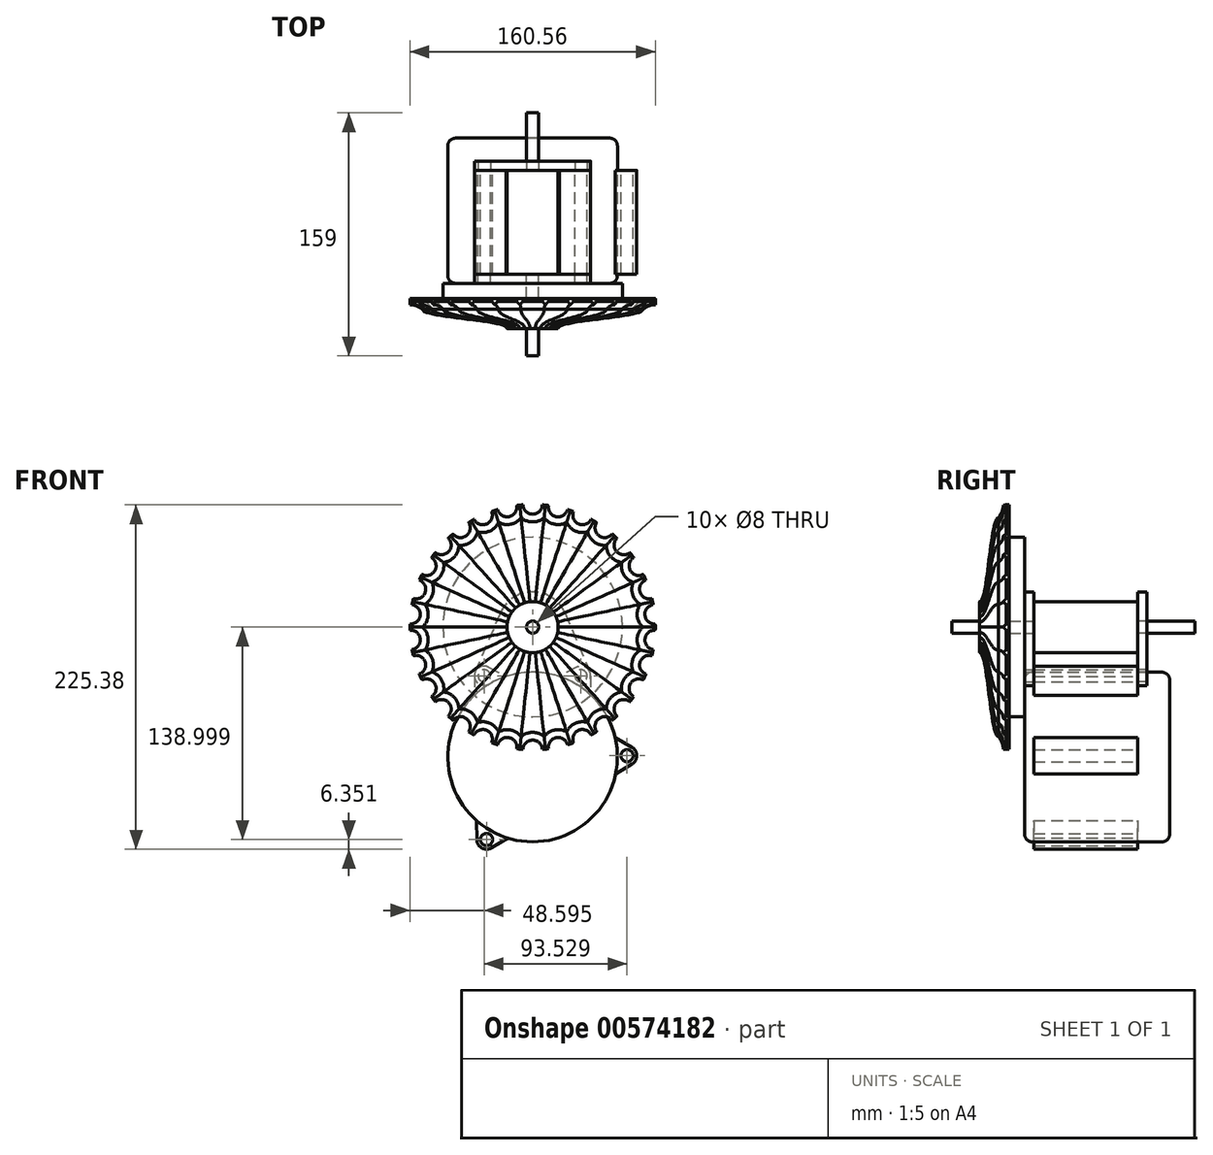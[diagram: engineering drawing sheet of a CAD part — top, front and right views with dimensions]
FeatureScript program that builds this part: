
annotation { "Feature Type Name" : "Feature", "Feature Type Description" : "" }
export const myFeature = defineFeature(function(context is Context, id is Id, definition is map)
    precondition{}
    {
        {
            var Q0;
            Q0=qCreatedBy(makeId("Front.planeOp"),FACE);
            var sketch = newSketch(context, id + "F0", { "sketchPlane" : qUnion([Q0])});
            skCircle(sketch, "E0", {"center": v(0, 0) * mm, "radius": 4 * mm});
            skCircle(sketch, "E1", {"center": v(0, 0) * mm, "radius": 16.75 * mm});
            skCircle(sketch, "E2", {"center": v(0, 0) * mm, "radius": 58.75 * mm, "construction": true});
            skLineSegment(sketch, "E3", {"start": v(0, 58.75) * mm, "end": v(0, -140.5) * mm, "construction": true});
            skCircle(sketch, "E4", {"center": v(0, -85) * mm, "radius": 55.5 * mm});
            skArc(sketch, "E5", {"start": v(28.43, -37.34) * mm, "mid": v(38.03, -32.02) * mm, "end": v(28.67, -26.3) * mm});
            skArc(sketch, "E6", {"start": v(-28.67, -26.3) * mm, "mid": v(-38.03, -32.02) * mm, "end": v(-28.43, -37.34) * mm});
            skArc(sketch, "E7.1.0", {"start": v(-36.5, -139.18) * mm, "mid": v(-33.25, -144.54) * mm, "end": v(-26.98, -144.5) * mm});
            skArc(sketch, "E7.2.0", {"start": v(65.17, -89.53) * mm, "mid": v(68.2, -84.03) * mm, "end": v(65.02, -78.62) * mm});
            skCircle(sketch, "E8", {"center": v(31.69, -31.88) * mm, "radius": 4 * mm});
            skCircle(sketch, "E9", {"center": v(-31.69, -31.88) * mm, "radius": 4 * mm});
            skCircle(sketch, "E10.1.0", {"center": v(-30.16, -139) * mm, "radius": 4 * mm});
            skCircle(sketch, "E10.2.0", {"center": v(61.84, -84.12) * mm, "radius": 4 * mm});
            skArc(sketch, "E11.0", {"start": v(21.27, 9) * mm, "mid": v(0, 23.1) * mm, "end": v(-21.27, 9) * mm});
            skLineSegment(sketch, "E12", {"start": v(-21.27, 9) * mm, "end": v(-37.53, -29.4) * mm});
            skLineSegment(sketch, "E13", {"start": v(21.27, 9) * mm, "end": v(37.53, -29.4) * mm});
            skLineSegment(sketch, "E14", {"start": v(-38.04, -31.88) * mm, "end": v(-38.04, -44.58) * mm});
            skLineSegment(sketch, "E15", {"start": v(-28.67, -26.3) * mm, "end": v(-17.5, -32.33) * mm});
            skLineSegment(sketch, "E16.1.0", {"start": v(-36.5, -139.18) * mm, "end": v(-36.87, -126.49) * mm});
            skLineSegment(sketch, "E16.1.1", {"start": v(-26.98, -144.5) * mm, "end": v(-15.99, -138.15) * mm});
            skLineSegment(sketch, "E16.2.0", {"start": v(65.17, -89.53) * mm, "end": v(54.36, -96.19) * mm});
            skLineSegment(sketch, "E16.2.1", {"start": v(65.02, -78.62) * mm, "end": v(54.02, -72.27) * mm});
            skLineSegment(sketch, "E17.MirrorCS", {"start": v(28.67, -26.3) * mm, "end": v(17.5, -32.33) * mm});
            skLineSegment(sketch, "E18.MirrorCS", {"start": v(38.04, -31.88) * mm, "end": v(38.04, -44.58) * mm});
            skSolve(sketch);
        }
        {
            var Q0;
            Q0=makeQuery(id+"F0.imprint","IMPRINT",FACE,{"disambiguationData":[TD([[makeQuery(id+"F0.imprint","IMPRINT",EDGE,{"derivedFrom":sQuery(id+"F0.wireOp",EDGE,"E0")}),1.0]])]});
            extrude(context, id + "F1", {"entities" : qUnion([Q0]), "depth" : 87.5 * mm, "offsetDistance" : 25.4 * mm, "hasSecondDirection" : true, "secondDirectionOppositeDirection" : true, "secondDirectionDepth" : 71.5 * mm});
        }
        {
            var Q0;
            Q0=makeQuery(id+"F0.imprint","IMPRINT",FACE,{"disambiguationData":[TD([[makeQuery(id+"F0.imprint","IMPRINT",EDGE,{"derivedFrom":sQuery(id+"F0.wireOp",EDGE,"E0")}),-1.0]])]});
            var Q1;
            {var subQ3=sQuery(id+"F0.wireOp",EDGE,"E14");Q1=makeQuery(id+"F0.imprint","IMPRINT",FACE,{"disambiguationData":[TD([[makeQuery(id+"F0.imprint","IMPRINT",EDGE,{"derivedFrom":subQ3}),1.0]])]});}
            var Q2;
            Q2=makeQuery(id+"F0.imprint","IMPRINT",FACE,{"disambiguationData":[TD([[makeQuery(id+"F0.imprint","IMPRINT",EDGE,{"derivedFrom":sQuery(id+"F0.wireOp",EDGE,"E9")}),-1.0]])]});
            var Q3;
            Q3=makeQuery(id+"F0.imprint","IMPRINT",FACE,{"disambiguationData":[TD([[makeQuery(id+"F0.imprint","IMPRINT",EDGE,{"derivedFrom":sQuery(id+"F0.wireOp",EDGE,"E8")}),-1.0]])]});
            var Q4;
            {var subQ3=sQuery(id+"F0.wireOp",EDGE,"E18.MirrorCS");Q4=makeQuery(id+"F0.imprint","IMPRINT",FACE,{"disambiguationData":[TD([[makeQuery(id+"F0.imprint","IMPRINT",EDGE,{"derivedFrom":subQ3}),-1.0]])]});}
            var Q5;
            Q5=makeQuery(id+"F0.imprint","IMPRINT",FACE,{"disambiguationData":[TD([[makeQuery(id+"F0.imprint","IMPRINT",EDGE,{"derivedFrom":sQuery(id+"F0.wireOp",EDGE,"E7.2.0")}),1.0]])]});
            var Q6;
            Q6=makeQuery(id+"F0.imprint","IMPRINT",FACE,{"disambiguationData":[TD([[makeQuery(id+"F0.imprint","IMPRINT",EDGE,{"derivedFrom":sQuery(id+"F0.wireOp",EDGE,"E7.1.0")}),1.0]])]});
            extrude(context, id + "F2", {"entities" : qUnion([Q0, Q1, Q2, Q3, Q4, Q5, Q6]), "operationType" : NewBodyOperationType.ADD, "depth" : 68 * mm, "offsetDistance" : 25.4 * mm, "symmetric" : true});
        }
        {
            var Q0;
            {var subQ0=sQuery(id+"F0.wireOp",EDGE,"E4");var subQ5=makeQuery(id+"F0.imprint","INTERSECT",VERTEX,{"derivedFrom":[subQ0,sQuery(id+"F0.wireOp",EDGE,"E16.2.1")]});Q0=makeQuery(id+"F0.imprint","IMPRINT",FACE,{"disambiguationData":[TD([[makeQuery(id+"F0.imprint","IMPRINT",EDGE,{"disambiguationData":[TD([[subQ5,-1.0]])],"derivedFrom":subQ0}),1.0]])]});}
            extrude(context, id + "F3", {"entities" : qUnion([Q0]), "depth" : 40 * mm, "offsetDistance" : 25.4 * mm, "hasSecondDirection" : true, "secondDirectionOppositeDirection" : true, "secondDirectionDepth" : 55 * mm});
        }
        {
            var Q0;
            Q0=makeQuery(id+"F3.opExtrude","CAP_EDGE",EDGE,{"disambiguationData":[OSD([sQuery(id+"F0.wireOp",EDGE,"E4")])],"isStart":false});
            var Q1;
            Q1=makeQuery(id+"F3.opExtrude","CAP_EDGE",EDGE,{"disambiguationData":[OSD([sQuery(id+"F0.wireOp",EDGE,"E4")])],"isStart":true});
            fillet(context, id + "F4", {"entities" : qUnion([Q0, Q1]), "radius" : 5.08 * mm, "tangentPropagation" : true, "allowEdgeOverflow" : false});
        }
        {
            var Q0;
            Q0=makeQuery(id+"F0.imprint","IMPRINT",FACE,{"disambiguationData":[TD([[makeQuery(id+"F0.imprint","IMPRINT",EDGE,{"derivedFrom":sQuery(id+"F0.wireOp",EDGE,"E0")}),-1.0]])]});
            var Q1;
            Q1=makeQuery(id+"F0.imprint","IMPRINT",FACE,{"disambiguationData":[TD([[makeQuery(id+"F0.imprint","IMPRINT",EDGE,{"derivedFrom":sQuery(id+"F0.wireOp",EDGE,"E1")}),-1.0]])]});
            var Q2;
            Q2=makeQuery(id+"F0.imprint","IMPRINT",FACE,{"disambiguationData":[TD([[makeQuery(id+"F0.imprint","IMPRINT",EDGE,{"derivedFrom":sQuery(id+"F0.wireOp",EDGE,"E9")}),-1.0]])]});
            var Q3;
            Q3=makeQuery(id+"F0.imprint","IMPRINT",FACE,{"disambiguationData":[TD([[makeQuery(id+"F0.imprint","IMPRINT",EDGE,{"derivedFrom":sQuery(id+"F0.wireOp",EDGE,"E8")}),-1.0]])]});
            var Q4;
            Q4=makeQuery(id+"F2.opExtrude","CAP_FACE",FACE,{"disambiguationData":[OSD([sQuery(id+"F0.wireOp",EDGE,"E4"),sQuery(id+"F0.wireOp",EDGE,"E6"),sQuery(id+"F0.wireOp",EDGE,"E9"),sQuery(id+"F0.wireOp",EDGE,"E14"),sQuery(id+"F0.wireOp",EDGE,"E15")])],"isStart":false});
            extrude(context, id + "F5", {"entities" : qUnion([Q0, Q1, Q2, Q3]), "depth" : 40 * mm, "offsetDistance" : 25.4 * mm, "hasSecondDirection" : true, "secondDirectionBound" : BoundingType.UP_TO_SURFACE, "secondDirectionOppositeDirection" : false, "secondDirectionDepth" : 25.4 * mm, "secondDirectionBoundEntityFace" : qUnion([Q4])});
        }
        {
            var Q0;
            Q0=makeQuery(id+"F5.opExtrude","SWEPT_BODY",BODY,{"disambiguationData":[OSD([sQuery(id+"F0.wireOp",EDGE,"E0"),sQuery(id+"F0.wireOp",EDGE,"E4"),sQuery(id+"F0.wireOp",EDGE,"E5"),sQuery(id+"F0.wireOp",EDGE,"E6"),sQuery(id+"F0.wireOp",EDGE,"E8"),sQuery(id+"F0.wireOp",EDGE,"E9"),sQuery(id+"F0.wireOp",EDGE,"E11.0"),sQuery(id+"F0.wireOp",EDGE,"E12"),sQuery(id+"F0.wireOp",EDGE,"E13")])]});
            var Q1;
            Q1=qCreatedBy(makeId("Front.planeOp"),FACE);
            mirror(context, id + "F6", {"entities" : qUnion([Q0]), "mirrorPlane" : qUnion([Q1])});
        }
        {
            var Q0;
            Q0=makeQuery(id+"F1.opExtrude","CAP_FACE",FACE,{"disambiguationData":[OSD([sQuery(id+"F0.wireOp",EDGE,"E0")])],"isStart":false});
            cPlane(context, id + "F7", {"entities" : qUnion([Q0]), "cplaneType" : CPlaneType.OFFSET, "offset" : 0 * mm, "width" : 152.4 * mm, "height" : 152.4 * mm});
        }
        {
            var Q0;
            Q0=qCreatedBy(id+"F7.planeOp",FACE);
            var sketch = newSketch(context, id + "F8", { "sketchPlane" : qUnion([Q0])});
            skCircle(sketch, "E19", {"center": v(0, 0) * mm, "radius": 58.75 * mm});
            skCircle(sketch, "E20", {"center": v(0, 0) * mm, "radius": 80.28 * mm});
            skCircle(sketch, "E21", {"center": v(0, 80.28) * mm, "radius": 6.35 * mm});
            skCircle(sketch, "E22.1.0", {"center": v(-16.7, 78.52) * mm, "radius": 6.35 * mm});
            skCircle(sketch, "E22.2.0", {"center": v(-32.65, 73.34) * mm, "radius": 6.35 * mm});
            skCircle(sketch, "E22.3.0", {"center": v(-47.19, 64.95) * mm, "radius": 6.35 * mm});
            skCircle(sketch, "E22.4.0", {"center": v(-59.66, 53.72) * mm, "radius": 6.35 * mm});
            skCircle(sketch, "E22.5.0", {"center": v(-69.52, 40.14) * mm, "radius": 6.35 * mm});
            skCircle(sketch, "E22.6.0", {"center": v(-76.35, 24.8) * mm, "radius": 6.35 * mm});
            skCircle(sketch, "E22.7.0", {"center": v(-79.84, 8.4) * mm, "radius": 6.35 * mm});
            skCircle(sketch, "E22.8.0", {"center": v(-79.84, -8.4) * mm, "radius": 6.35 * mm});
            skCircle(sketch, "E22.9.0", {"center": v(-76.35, -24.8) * mm, "radius": 6.35 * mm});
            skCircle(sketch, "E22.10.0", {"center": v(-69.52, -40.14) * mm, "radius": 6.35 * mm});
            skCircle(sketch, "E22.11.0", {"center": v(-59.66, -53.72) * mm, "radius": 6.35 * mm});
            skCircle(sketch, "E22.12.0", {"center": v(-47.19, -64.95) * mm, "radius": 6.35 * mm});
            skCircle(sketch, "E22.13.0", {"center": v(-32.65, -73.34) * mm, "radius": 6.35 * mm});
            skCircle(sketch, "E22.14.0", {"center": v(-16.7, -78.52) * mm, "radius": 6.35 * mm});
            skCircle(sketch, "E22.15.0", {"center": v(0, -80.28) * mm, "radius": 6.35 * mm});
            skCircle(sketch, "E22.16.0", {"center": v(16.7, -78.52) * mm, "radius": 6.35 * mm});
            skCircle(sketch, "E22.17.0", {"center": v(32.65, -73.34) * mm, "radius": 6.35 * mm});
            skCircle(sketch, "E22.18.0", {"center": v(47.19, -64.95) * mm, "radius": 6.35 * mm});
            skCircle(sketch, "E22.19.0", {"center": v(59.66, -53.72) * mm, "radius": 6.35 * mm});
            skCircle(sketch, "E22.20.0", {"center": v(69.52, -40.14) * mm, "radius": 6.35 * mm});
            skCircle(sketch, "E22.21.0", {"center": v(76.35, -24.8) * mm, "radius": 6.35 * mm});
            skCircle(sketch, "E22.22.0", {"center": v(79.84, -8.4) * mm, "radius": 6.35 * mm});
            skCircle(sketch, "E22.23.0", {"center": v(79.84, 8.4) * mm, "radius": 6.35 * mm});
            skCircle(sketch, "E22.24.0", {"center": v(76.35, 24.8) * mm, "radius": 6.35 * mm});
            skCircle(sketch, "E22.25.0", {"center": v(69.52, 40.14) * mm, "radius": 6.35 * mm});
            skCircle(sketch, "E22.26.0", {"center": v(59.66, 53.72) * mm, "radius": 6.35 * mm});
            skCircle(sketch, "E22.27.0", {"center": v(47.19, 64.95) * mm, "radius": 6.35 * mm});
            skCircle(sketch, "E22.28.0", {"center": v(32.65, 73.34) * mm, "radius": 6.35 * mm});
            skCircle(sketch, "E22.29.0", {"center": v(16.7, 78.52) * mm, "radius": 6.35 * mm});
            skSolve(sketch);
        }
        {
            var Q0;
            Q0=makeQuery(id+"F8.imprint","IMPRINT",FACE,{"disambiguationData":[TD([[makeQuery(id+"F8.imprint","IMPRINT",EDGE,{"derivedFrom":sQuery(id+"F8.wireOp",EDGE,"E19")}),1.0]])]});
            extrude(context, id + "F9", {"entities" : qUnion([Q0]), "oppositeDirection" : true, "depth" : 47.5 * mm, "offsetDistance" : 25.4 * mm, "hasSecondDirection" : true, "secondDirectionOppositeDirection" : true, "secondDirectionDepth" : 37.5 * mm});
        }
        {
            var Q0;
            Q0=makeQuery(id+"F8.imprint","IMPRINT",FACE,{"disambiguationData":[TD([[makeQuery(id+"F8.imprint","IMPRINT",EDGE,{"derivedFrom":sQuery(id+"F8.wireOp",EDGE,"E19")}),-1.0]])]});
            var Q1;
            Q1=makeQuery(id+"F8.imprint","IMPRINT",FACE,{"disambiguationData":[TD([[makeQuery(id+"F8.imprint","IMPRINT",EDGE,{"derivedFrom":sQuery(id+"F8.wireOp",EDGE,"E19")}),1.0]])]});
            var Q2;
            Q2=makeQuery(id+"F9.opExtrude","CAP_FACE",FACE,{"disambiguationData":[OSD([sQuery(id+"F8.wireOp",EDGE,"E19")])],"isStart":true});
            extrude(context, id + "F10", {"entities" : qUnion([Q0, Q1]), "endBound" : BoundingType.UP_TO_SURFACE, "oppositeDirection" : true, "depth" : 25.4 * mm, "endBoundEntityFace" : qUnion([Q2]), "offsetDistance" : 25.4 * mm, "hasSecondDirection" : true, "secondDirectionOppositeDirection" : true, "secondDirectionDepth" : 30.48 * mm});
        }
        {
            var Q0;
            Q0=makeQuery(id+"F1.opExtrude","CAP_FACE",FACE,{"disambiguationData":[OSD([sQuery(id+"F0.wireOp",EDGE,"E0")])],"isStart":false});
            cPlane(context, id + "F11", {"entities" : qUnion([Q0]), "cplaneType" : CPlaneType.OFFSET, "offset" : 18 * mm, "oppositeDirection" : true, "width" : 152.4 * mm, "height" : 152.4 * mm});
        }
        {
            var Q0;
            Q0=qCreatedBy(id+"F11.planeOp",FACE);
            var sketch = newSketch(context, id + "F12", { "sketchPlane" : qUnion([Q0])});
            skCircle(sketch, "E23", {"center": v(0, 0) * mm, "radius": 16.75 * mm});
            skSolve(sketch);
        }
        {
            var Q0;
            Q0=makeQuery(id+"F10.opExtrude","CAP_FACE",FACE,{"disambiguationData":[OSD([sQuery(id+"F8.wireOp",EDGE,"E20"),sQuery(id+"F8.wireOp",EDGE,"E21"),sQuery(id+"F8.wireOp",EDGE,"E22.1.0"),sQuery(id+"F8.wireOp",EDGE,"E22.2.0"),sQuery(id+"F8.wireOp",EDGE,"E22.3.0"),sQuery(id+"F8.wireOp",EDGE,"E22.4.0"),sQuery(id+"F8.wireOp",EDGE,"E22.5.0"),sQuery(id+"F8.wireOp",EDGE,"E22.6.0"),sQuery(id+"F8.wireOp",EDGE,"E22.7.0"),sQuery(id+"F8.wireOp",EDGE,"E22.8.0"),sQuery(id+"F8.wireOp",EDGE,"E22.9.0"),sQuery(id+"F8.wireOp",EDGE,"E22.10.0"),sQuery(id+"F8.wireOp",EDGE,"E22.11.0"),sQuery(id+"F8.wireOp",EDGE,"E22.12.0"),sQuery(id+"F8.wireOp",EDGE,"E22.13.0"),sQuery(id+"F8.wireOp",EDGE,"E22.14.0"),sQuery(id+"F8.wireOp",EDGE,"E22.15.0"),sQuery(id+"F8.wireOp",EDGE,"E22.16.0"),sQuery(id+"F8.wireOp",EDGE,"E22.17.0"),sQuery(id+"F8.wireOp",EDGE,"E22.18.0"),sQuery(id+"F8.wireOp",EDGE,"E22.19.0"),sQuery(id+"F8.wireOp",EDGE,"E22.20.0"),sQuery(id+"F8.wireOp",EDGE,"E22.21.0"),sQuery(id+"F8.wireOp",EDGE,"E22.22.0"),sQuery(id+"F8.wireOp",EDGE,"E22.23.0"),sQuery(id+"F8.wireOp",EDGE,"E22.24.0"),sQuery(id+"F8.wireOp",EDGE,"E22.25.0"),sQuery(id+"F8.wireOp",EDGE,"E22.26.0"),sQuery(id+"F8.wireOp",EDGE,"E22.27.0"),sQuery(id+"F8.wireOp",EDGE,"E22.28.0"),sQuery(id+"F8.wireOp",EDGE,"E22.29.0")])],"isStart":true});
            chamfer(context, id + "F13", {"entities" : qUnion([Q0]), "width" : 5.08 * mm, "tangentPropagation" : true});
        }
        {
            var Q1;
            Q1=makeQuery(id+"F10.opExtrude","CAP_FACE",FACE,{"disambiguationData":[OSD([sQuery(id+"F8.wireOp",EDGE,"E20"),sQuery(id+"F8.wireOp",EDGE,"E21"),sQuery(id+"F8.wireOp",EDGE,"E22.1.0"),sQuery(id+"F8.wireOp",EDGE,"E22.2.0"),sQuery(id+"F8.wireOp",EDGE,"E22.3.0"),sQuery(id+"F8.wireOp",EDGE,"E22.4.0"),sQuery(id+"F8.wireOp",EDGE,"E22.5.0"),sQuery(id+"F8.wireOp",EDGE,"E22.6.0"),sQuery(id+"F8.wireOp",EDGE,"E22.7.0"),sQuery(id+"F8.wireOp",EDGE,"E22.8.0"),sQuery(id+"F8.wireOp",EDGE,"E22.9.0"),sQuery(id+"F8.wireOp",EDGE,"E22.10.0"),sQuery(id+"F8.wireOp",EDGE,"E22.11.0"),sQuery(id+"F8.wireOp",EDGE,"E22.12.0"),sQuery(id+"F8.wireOp",EDGE,"E22.13.0"),sQuery(id+"F8.wireOp",EDGE,"E22.14.0"),sQuery(id+"F8.wireOp",EDGE,"E22.15.0"),sQuery(id+"F8.wireOp",EDGE,"E22.16.0"),sQuery(id+"F8.wireOp",EDGE,"E22.17.0"),sQuery(id+"F8.wireOp",EDGE,"E22.18.0"),sQuery(id+"F8.wireOp",EDGE,"E22.19.0"),sQuery(id+"F8.wireOp",EDGE,"E22.20.0"),sQuery(id+"F8.wireOp",EDGE,"E22.21.0"),sQuery(id+"F8.wireOp",EDGE,"E22.22.0"),sQuery(id+"F8.wireOp",EDGE,"E22.23.0"),sQuery(id+"F8.wireOp",EDGE,"E22.24.0"),sQuery(id+"F8.wireOp",EDGE,"E22.25.0"),sQuery(id+"F8.wireOp",EDGE,"E22.26.0"),sQuery(id+"F8.wireOp",EDGE,"E22.27.0"),sQuery(id+"F8.wireOp",EDGE,"E22.28.0"),sQuery(id+"F8.wireOp",EDGE,"E22.29.0")])],"isStart":true});
            var Q2;
            Q2=makeQuery(id+"F12.imprint","IMPRINT",FACE,{"disambiguationData":[TD([[makeQuery(id+"F12.imprint","IMPRINT",EDGE,{"derivedFrom":sQuery(id+"F12.wireOp",EDGE,"E23")}),1.0]])]});
            loft(context, id + "F14", {"operationType" : NewBodyOperationType.ADD, "startCondition" : LoftEndDerivativeType.NORMAL_TO_PROFILE, "startMagnitude" : 1, "endCondition" : LoftEndDerivativeType.NORMAL_TO_PROFILE, "endMagnitude" : 1, "sheetProfilesArray" : [{ "sheetProfileEntities" : qUnion([Q1]) }, { "sheetProfileEntities" : qUnion([Q2]) }]});
        }
    });
